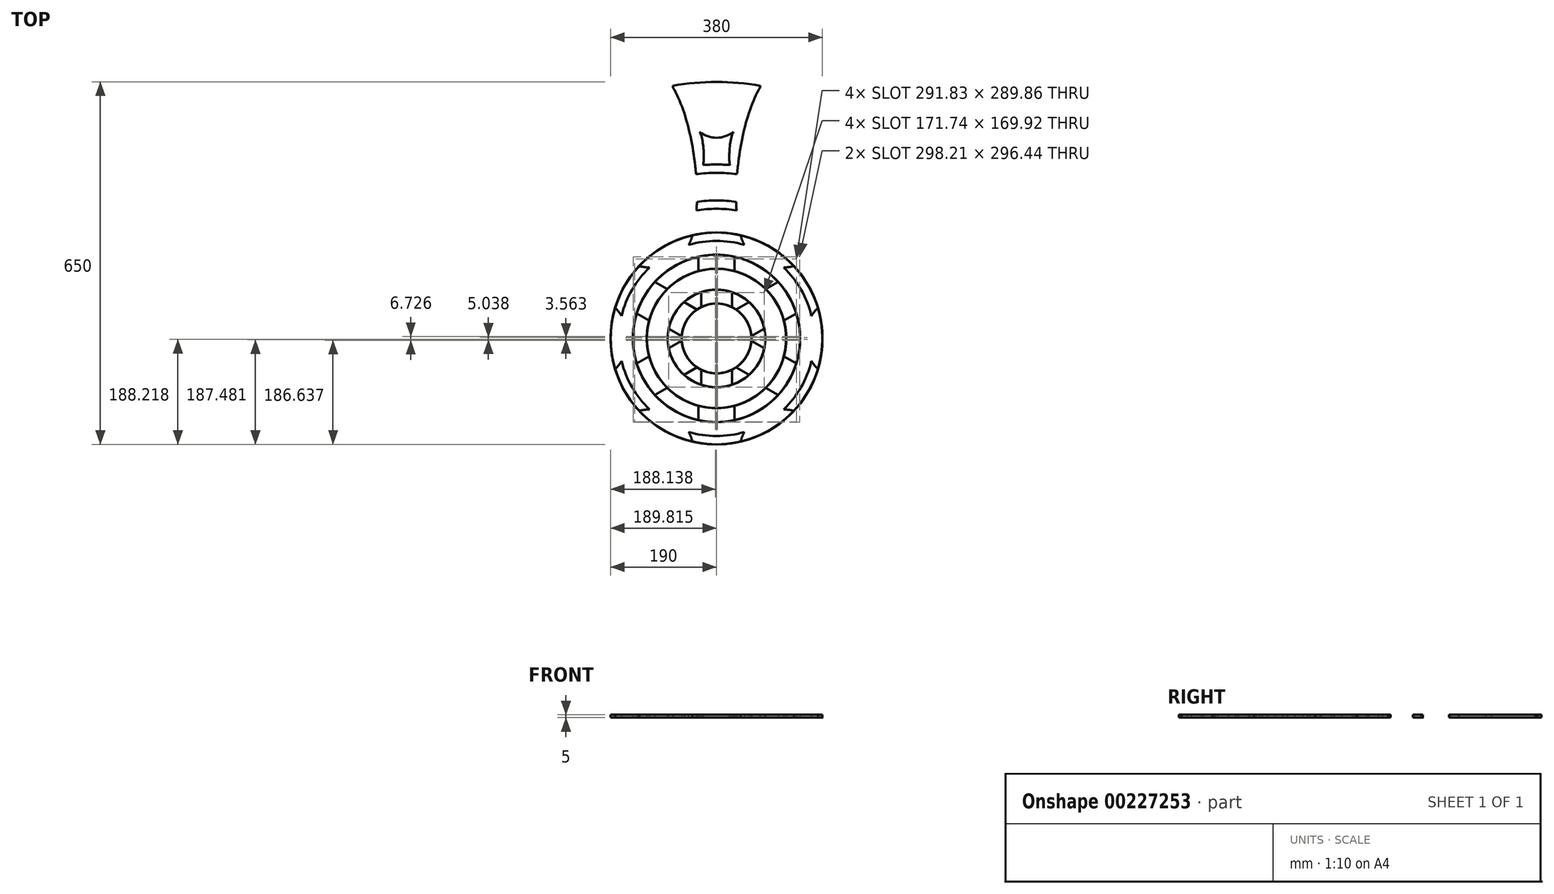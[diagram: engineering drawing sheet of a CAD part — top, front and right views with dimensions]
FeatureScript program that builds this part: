
annotation { "Feature Type Name" : "Feature", "Feature Type Description" : "" }
export const myFeature = defineFeature(function(context is Context, id is Id, definition is map)
    precondition{}
    {
        {
            var Q0;
            Q0=qCreatedBy(makeId("Top.planeOp"),FACE);
            var sketch = newSketch(context, id + "F0", { "sketchPlane" : qUnion([Q0])});
            skCircle(sketch, "E0", {"center": v(0, 0) * mm, "radius": 175 * mm});
            skCircle(sketch, "E1", {"center": v(0, 0) * mm, "radius": 150 * mm});
            skCircle(sketch, "E2", {"center": v(0, 0) * mm, "radius": 125 * mm});
            skLineSegment(sketch, "E3", {"start": v(-32.5, 120.7) * mm, "end": v(-32.5, 146.44) * mm});
            skLineSegment(sketch, "E4.MirrorCS", {"start": v(32.5, 120.7) * mm, "end": v(32.5, 146.44) * mm});
            skCircle(sketch, "E5", {"center": v(0, 0) * mm, "radius": 460 * mm});
            skFitSpline(sketch, "E6", {"points": [v(-50, 167.7) * mm, v(-80, 453) * mm], "startDerivative": vector(88.18, 161) * mm, "endDerivative": vector(-129.3, 202.35) * mm});
            skFitSpline(sketch, "E7.MirrorCS", {"points": [v(50, 167.7) * mm, v(80, 453) * mm], "startDerivative": vector(-88.18, 161) * mm, "endDerivative": vector(129.3, 202.35) * mm});
            skCircle(sketch, "E8", {"center": v(0, 0) * mm, "radius": 87.5 * mm});
            skCircle(sketch, "E9", {"center": v(0, 0) * mm, "radius": 62.5 * mm});
            skLineSegment(sketch, "E10", {"start": v(-27.5, 83.07) * mm, "end": v(-27.5, 56.12) * mm});
            skLineSegment(sketch, "E11.MirrorCS", {"start": v(27.5, 83.07) * mm, "end": v(27.5, 56.12) * mm});
            skLineSegment(sketch, "E12", {"start": v(0, 460) * mm, "end": v(0, 175) * mm, "construction": true});
            skCircle(sketch, "E13", {"center": v(0, 410) * mm, "radius": 40.5 * mm});
            skCircle(sketch, "E14", {"center": v(0, 410) * mm, "radius": 50 * mm});
            skCircle(sketch, "E15", {"center": v(0, 0) * mm, "radius": 311.98 * mm});
            skFitSpline(sketch, "E16", {"points": [v(-30.43, 370.33) * mm, v(-24.32, 311.03) * mm], "startDerivative": vector(22.47, -28.06) * mm, "endDerivative": vector(-9, -16.24) * mm});
            skFitSpline(sketch, "E17", {"points": [v(-7.2, 360.52) * mm, v(-7.09, 311.9) * mm], "startDerivative": vector(4.93, -10.05) * mm, "endDerivative": vector(-4.34, -12.32) * mm});
            skCircle(sketch, "E18", {"center": v(0, 0) * mm, "radius": 296.98 * mm});
            skCircle(sketch, "E19", {"center": v(0, 0) * mm, "radius": 247.51 * mm});
            skCircle(sketch, "E20", {"center": v(0, 0) * mm, "radius": 232.51 * mm});
            skFitSpline(sketch, "E21", {"points": [v(-25.41, 295.9) * mm, v(-21.84, 246.55) * mm], "startDerivative": vector(9.96, -56.26) * mm, "endDerivative": vector(0.38, -40.34) * mm});
            skFitSpline(sketch, "E22", {"points": [v(-8.68, 296.86) * mm, v(-8.65, 247.36) * mm], "startDerivative": vector(8.12, -39.94) * mm, "endDerivative": vector(-8.84, -46.89) * mm});
            skCircle(sketch, "E23", {"center": v(0, 0) * mm, "radius": 190 * mm});
            skFitSpline(sketch, "E24", {"points": [v(-22.58, 231.41) * mm, v(-30.02, 187.61) * mm], "startDerivative": vector(1.14, -45.94) * mm, "endDerivative": vector(-12.77, -38.05) * mm});
            skFitSpline(sketch, "E25", {"points": [v(-10.28, 232.28) * mm, v(-12.5, 189.59) * mm], "startDerivative": vector(3.08, -41) * mm, "endDerivative": vector(-10.11, -38.75) * mm});
            skFitSpline(sketch, "E26.MirrorCS", {"points": [v(25.41, 295.9) * mm, v(21.84, 246.55) * mm], "startDerivative": vector(-9.96, -56.26) * mm, "endDerivative": vector(-0.38, -40.34) * mm});
            skFitSpline(sketch, "E27.MirrorCS", {"points": [v(8.68, 296.86) * mm, v(8.65, 247.36) * mm], "startDerivative": vector(-8.12, -39.94) * mm, "endDerivative": vector(8.84, -46.89) * mm});
            skFitSpline(sketch, "E28.MirrorCS", {"points": [v(30.43, 370.33) * mm, v(24.32, 311.03) * mm], "startDerivative": vector(-22.47, -28.06) * mm, "endDerivative": vector(9, -16.24) * mm});
            skFitSpline(sketch, "E29.MirrorCS", {"points": [v(7.2, 360.52) * mm, v(7.09, 311.9) * mm], "startDerivative": vector(-4.93, -10.05) * mm, "endDerivative": vector(4.34, -12.32) * mm});
            skFitSpline(sketch, "E30.MirrorCS", {"points": [v(22.58, 231.41) * mm, v(30.02, 187.61) * mm], "startDerivative": vector(-1.14, -45.94) * mm, "endDerivative": vector(12.77, -38.05) * mm});
            skFitSpline(sketch, "E31.MirrorCS", {"points": [v(10.28, 232.28) * mm, v(12.5, 189.59) * mm], "startDerivative": vector(-3.08, -41) * mm, "endDerivative": vector(10.11, -38.75) * mm});
            skLineSegment(sketch, "E32", {"start": v(-18.4, 148.87) * mm, "end": v(-18.4, 123.64) * mm});
            skLineSegment(sketch, "E33", {"start": v(-8.48, 149.76) * mm, "end": v(-8.48, 124.71) * mm});
            skLineSegment(sketch, "E34.MirrorCS", {"start": v(8.48, 149.76) * mm, "end": v(8.48, 124.71) * mm});
            skLineSegment(sketch, "E35.MirrorCS", {"start": v(18.4, 148.87) * mm, "end": v(18.4, 123.64) * mm});
            skLineSegment(sketch, "E36", {"start": v(-15.12, 86.18) * mm, "end": v(-15.12, 60.64) * mm});
            skLineSegment(sketch, "E37", {"start": v(-7.04, 87.22) * mm, "end": v(-7.04, 62.1) * mm});
            skLineSegment(sketch, "E38.MirrorCS", {"start": v(7.04, 87.22) * mm, "end": v(7.04, 62.1) * mm});
            skLineSegment(sketch, "E39.MirrorCS", {"start": v(15.12, 86.18) * mm, "end": v(15.12, 60.64) * mm});
            skCircle(sketch, "E40", {"center": v(0, 0) * mm, "radius": 451.5 * mm});
            skFitSpline(sketch, "E41", {"points": [v(-71.38, 445.82) * mm, v(-49.39, 417.81) * mm], "startDerivative": vector(31.6, -15.2) * mm, "endDerivative": vector(2.84, -34.22) * mm});
            skFitSpline(sketch, "E42.MirrorCS", {"points": [v(71.38, 445.82) * mm, v(49.39, 417.81) * mm], "startDerivative": vector(-31.6, -15.2) * mm, "endDerivative": vector(-2.84, -34.22) * mm});
            skFitSpline(sketch, "E43", {"points": [v(-77.8, 449.43) * mm, v(-67.79, 454.98) * mm], "startDerivative": vector(-6.69, 25.98) * mm, "endDerivative": vector(20.18, 3.16) * mm});
            skFitSpline(sketch, "E44.MirrorCS", {"points": [v(77.8, 449.43) * mm, v(67.79, 454.98) * mm], "startDerivative": vector(6.69, 25.98) * mm, "endDerivative": vector(-20.18, 3.16) * mm});
            skFitSpline(sketch, "E45", {"points": [v(-65.6, 442.4) * mm, v(-58.32, 447.72) * mm], "startDerivative": vector(-4.19, 7.83) * mm, "endDerivative": vector(14.85, 7.1) * mm});
            skFitSpline(sketch, "E46.MirrorCS", {"points": [v(65.6, 442.4) * mm, v(58.32, 447.72) * mm], "startDerivative": vector(4.19, 7.83) * mm, "endDerivative": vector(-14.85, 7.1) * mm});
            skSolve(sketch);
        }
        {
            var Q0;
            Q0=makeQuery(id+"F0.imprint","IMPRINT",FACE,{"disambiguationData":[TD([[makeQuery(id+"F0.imprint","IMPRINT",EDGE,{"derivedFrom":sQuery(id+"F0.wireOp",EDGE,"E0")}),1.0]])]});
            var Q1;
            Q1=makeQuery(id+"F0.imprint","IMPRINT",FACE,{"disambiguationData":[TD([[makeQuery(id+"F0.imprint","IMPRINT",EDGE,{"derivedFrom":sQuery(id+"F0.wireOp",EDGE,"E2")}),1.0]])]});
            var Q2;
            Q2=makeQuery(id+"F0.imprint","IMPRINT",FACE,{"disambiguationData":[TD([[makeQuery(id+"F0.imprint","IMPRINT",EDGE,{"derivedFrom":sQuery(id+"F0.wireOp",EDGE,"E0")}),-1.0]])]});
            var Q3;
            {var subQ0=sQuery(id+"F0.wireOp",EDGE,"E3");Q3=makeQuery(id+"F0.imprint","IMPRINT",FACE,{"disambiguationData":[TD([[makeQuery(id+"F0.imprint","IMPRINT",EDGE,{"derivedFrom":subQ0}),-1.0]])]});}
            var Q4;
            {var subQ0=sQuery(id+"F0.wireOp",EDGE,"E9");var subQ1=makeQuery(id+"F0.imprint","INTERSECT",VERTEX,{"derivedFrom":[subQ0,sQuery(id+"F0.wireOp",EDGE,"E10")]});Q4=makeQuery(id+"F0.imprint","IMPRINT",FACE,{"disambiguationData":[TD([[makeQuery(id+"F0.imprint","IMPRINT",EDGE,{"disambiguationData":[TD([[subQ1,1.0]])],"derivedFrom":subQ0}),1.0]])]});}
            var Q5;
            {var subQ0=sQuery(id+"F0.wireOp",EDGE,"E10");Q5=makeQuery(id+"F0.imprint","IMPRINT",FACE,{"disambiguationData":[TD([[makeQuery(id+"F0.imprint","IMPRINT",EDGE,{"derivedFrom":subQ0}),1.0]])]});}
            var Q6;
            {var subQ1=sQuery(id+"F0.wireOp",EDGE,"E0");var subQ6=sQuery(id+"F0.wireOp",EDGE,"E6");var subQ7=makeQuery(id+"F0.imprint","INTERSECT",VERTEX,{"derivedFrom":[subQ1,subQ6]});Q6=makeQuery(id+"F0.imprint","IMPRINT",FACE,{"disambiguationData":[TD([[makeQuery(id+"F0.imprint","IMPRINT",EDGE,{"disambiguationData":[TD([[subQ7,-1.0]])],"derivedFrom":subQ1}),1.0]])]});}
            var Q7;
            {var subQ5=sQuery(id+"F0.wireOp",EDGE,"E17");Q7=makeQuery(id+"F0.imprint","IMPRINT",FACE,{"disambiguationData":[TD([[makeQuery(id+"F0.imprint","IMPRINT",EDGE,{"derivedFrom":subQ5}),1.0]])]});}
            var Q8;
            Q8=makeQuery(id+"F0.imprint","IMPRINT",FACE,{"disambiguationData":[TD([[makeQuery(id+"F0.imprint","IMPRINT",EDGE,{"derivedFrom":sQuery(id+"F0.wireOp",EDGE,"E13")}),-1.0]])]});
            var Q9;
            {var subQ0=sQuery(id+"F0.wireOp",EDGE,"E16");Q9=makeQuery(id+"F0.imprint","IMPRINT",FACE,{"disambiguationData":[TD([[makeQuery(id+"F0.imprint","IMPRINT",EDGE,{"derivedFrom":subQ0}),-1.0]])]});}
            var Q10;
            {var subQ5=sQuery(id+"F0.wireOp",EDGE,"E18");var subQ9=sQuery(id+"F0.wireOp",EDGE,"E6");var subQ10=makeQuery(id+"F0.imprint","INTERSECT",VERTEX,{"derivedFrom":[subQ9,subQ5]});Q10=makeQuery(id+"F0.imprint","IMPRINT",FACE,{"disambiguationData":[TD([[makeQuery(id+"F0.imprint","IMPRINT",EDGE,{"disambiguationData":[TD([[subQ10,-1.0]])],"derivedFrom":subQ9}),-1.0]])]});}
            var Q11;
            {var subQ5=sQuery(id+"F0.wireOp",EDGE,"E22");Q11=makeQuery(id+"F0.imprint","IMPRINT",FACE,{"disambiguationData":[TD([[makeQuery(id+"F0.imprint","IMPRINT",EDGE,{"derivedFrom":subQ5}),1.0]])]});}
            var Q12;
            {var subQ4=sQuery(id+"F0.wireOp",EDGE,"E20");var subQ7=sQuery(id+"F0.wireOp",EDGE,"E6");var subQ8=makeQuery(id+"F0.imprint","INTERSECT",VERTEX,{"derivedFrom":[subQ7,subQ4]});Q12=makeQuery(id+"F0.imprint","IMPRINT",FACE,{"disambiguationData":[TD([[makeQuery(id+"F0.imprint","IMPRINT",EDGE,{"disambiguationData":[TD([[subQ8,-1.0]])],"derivedFrom":subQ7}),-1.0]])]});}
            var Q13;
            {var subQ5=sQuery(id+"F0.wireOp",EDGE,"E25");Q13=makeQuery(id+"F0.imprint","IMPRINT",FACE,{"disambiguationData":[TD([[makeQuery(id+"F0.imprint","IMPRINT",EDGE,{"derivedFrom":subQ5}),1.0]])]});}
            var Q14;
            {var subQ5=sQuery(id+"F0.wireOp",EDGE,"E26.MirrorCS");Q14=makeQuery(id+"F0.imprint","IMPRINT",FACE,{"disambiguationData":[TD([[makeQuery(id+"F0.imprint","IMPRINT",EDGE,{"derivedFrom":subQ5}),1.0]])]});}
            var Q15;
            {var subQ5=sQuery(id+"F0.wireOp",EDGE,"E30.MirrorCS");Q15=makeQuery(id+"F0.imprint","IMPRINT",FACE,{"disambiguationData":[TD([[makeQuery(id+"F0.imprint","IMPRINT",EDGE,{"derivedFrom":subQ5}),1.0]])]});}
            var Q16;
            {var subQ0=sQuery(id+"F0.wireOp",EDGE,"E33");Q16=makeQuery(id+"F0.imprint","IMPRINT",FACE,{"disambiguationData":[TD([[makeQuery(id+"F0.imprint","IMPRINT",EDGE,{"derivedFrom":subQ0}),1.0]])]});}
            var Q17;
            {var subQ0=sQuery(id+"F0.wireOp",EDGE,"E4.MirrorCS");Q17=makeQuery(id+"F0.imprint","IMPRINT",FACE,{"disambiguationData":[TD([[makeQuery(id+"F0.imprint","IMPRINT",EDGE,{"derivedFrom":subQ0}),1.0]])]});}
            var Q18;
            Q18=makeQuery(id+"F0.imprint","IMPRINT",FACE,{"disambiguationData":[TD([[makeQuery(id+"F0.imprint","IMPRINT",EDGE,{"derivedFrom":sQuery(id+"F0.wireOp",EDGE,"E13")}),1.0]])]});
            var Q19;
            {var subQ0=sQuery(id+"F0.wireOp",EDGE,"E11.MirrorCS");Q19=makeQuery(id+"F0.imprint","IMPRINT",FACE,{"disambiguationData":[TD([[makeQuery(id+"F0.imprint","IMPRINT",EDGE,{"derivedFrom":subQ0}),-1.0]])]});}
            var Q20;
            {var subQ0=sQuery(id+"F0.wireOp",EDGE,"E37");Q20=makeQuery(id+"F0.imprint","IMPRINT",FACE,{"disambiguationData":[TD([[makeQuery(id+"F0.imprint","IMPRINT",EDGE,{"derivedFrom":subQ0}),1.0]])]});}
            var Q21;
            {var subQ0=sQuery(id+"F0.wireOp",EDGE,"E14");var subQ1=makeQuery(id+"F0.imprint","INTERSECT",VERTEX,{"derivedFrom":[sQuery(id+"F0.wireOp",EDGE,"E5"),subQ0]});Q21=makeQuery(id+"F0.imprint","IMPRINT",FACE,{"disambiguationData":[TD([[makeQuery(id+"F0.imprint","IMPRINT",EDGE,{"disambiguationData":[TD([[subQ1,1.0]])],"derivedFrom":subQ0}),1.0]])]});}
            var Q22;
            {var subQ2=sQuery(id+"F0.wireOp",EDGE,"E43");var subQ5=sQuery(id+"F0.wireOp",EDGE,"E5");var subQ8=makeQuery(id+"F0.imprint","INTERSECT",VERTEX,{"derivedFrom":[subQ5,subQ2]});Q22=makeQuery(id+"F0.imprint","IMPRINT",FACE,{"disambiguationData":[TD([[makeQuery(id+"F0.imprint","IMPRINT",EDGE,{"disambiguationData":[TD([[subQ8,1.0]])],"derivedFrom":subQ5}),1.0]])]});}
            var Q23;
            {var subQ2=sQuery(id+"F0.wireOp",EDGE,"E44.MirrorCS");var subQ6=sQuery(id+"F0.wireOp",EDGE,"E5");var subQ8=makeQuery(id+"F0.imprint","INTERSECT",VERTEX,{"derivedFrom":[subQ6,subQ2]});Q23=makeQuery(id+"F0.imprint","IMPRINT",FACE,{"disambiguationData":[TD([[makeQuery(id+"F0.imprint","IMPRINT",EDGE,{"disambiguationData":[TD([[subQ8,-1.0]])],"derivedFrom":subQ6}),1.0]])]});}
            var Q24;
            {var subQ5=sQuery(id+"F0.wireOp",EDGE,"E21");Q24=makeQuery(id+"F0.imprint","IMPRINT",FACE,{"disambiguationData":[TD([[makeQuery(id+"F0.imprint","IMPRINT",EDGE,{"derivedFrom":subQ5}),-1.0]])]});}
            var Q25;
            {var subQ5=sQuery(id+"F0.wireOp",EDGE,"E24");Q25=makeQuery(id+"F0.imprint","IMPRINT",FACE,{"disambiguationData":[TD([[makeQuery(id+"F0.imprint","IMPRINT",EDGE,{"derivedFrom":subQ5}),-1.0]])]});}
            var Q26;
            {var subQ3=sQuery(id+"F0.wireOp",EDGE,"E45");Q26=makeQuery(id+"F0.imprint","IMPRINT",FACE,{"disambiguationData":[TD([[makeQuery(id+"F0.imprint","IMPRINT",EDGE,{"derivedFrom":subQ3}),1.0]])]});}
            var Q27;
            {var subQ0=sQuery(id+"F0.wireOp",EDGE,"E28.MirrorCS");Q27=makeQuery(id+"F0.imprint","IMPRINT",FACE,{"disambiguationData":[TD([[makeQuery(id+"F0.imprint","IMPRINT",EDGE,{"derivedFrom":subQ0}),1.0]])]});}
            var Q28;
            {var subQ3=sQuery(id+"F0.wireOp",EDGE,"E46.MirrorCS");Q28=makeQuery(id+"F0.imprint","IMPRINT",FACE,{"disambiguationData":[TD([[makeQuery(id+"F0.imprint","IMPRINT",EDGE,{"derivedFrom":subQ3}),-1.0]])]});}
            extrude(context, id + "F1", {"entities" : qUnion([Q0, Q1, Q2, Q3, Q4, Q5, Q6, Q7, Q8, Q9, Q10, Q11, Q12, Q13, Q14, Q15, Q16, Q17, Q18, Q19, Q20, Q21, Q22, Q23, Q24, Q25, Q26, Q27, Q28]), "depth" : 5 * mm});
        }
        {
            var Q0;
            Q0=makeQuery(id+"F1.opExtrude","SWEPT_BODY",BODY,{"disambiguationData":[OSD([sQuery(id+"F0.wireOp",EDGE,"E2"),sQuery(id+"F0.wireOp",EDGE,"E3"),sQuery(id+"F0.wireOp",EDGE,"E0"),sQuery(id+"F0.wireOp",EDGE,"E1"),sQuery(id+"F0.wireOp",EDGE,"E4.MirrorCS")])]});
            var Q1;
            {var subQ0=sQuery(id+"F0.wireOp",EDGE,"E1");Q1=makeQuery(id+"F1.opExtrude","SWEPT_FACE",FACE,{"disambiguationData":[OSD([subQ0]),TDD([makeQuery(id+"F0.imprint","IMPRINT",EDGE,{"disambiguationData":[TD([[makeQuery(id+"F0.imprint","INTERSECT",VERTEX,{"derivedFrom":[sQuery(id+"F0.wireOp",EDGE,"E3"),subQ0]}),1.0]])],"derivedFrom":subQ0})])]});}
            circularPattern(context, id + "F2", {"operationType" : NewBodyOperationType.ADD, "entities" : qUnion([Q0]), "axis" : qUnion([Q1]), "angle" : 360 * degree, "instanceCount" : 6, "equalSpace" : true});
        }
    });
